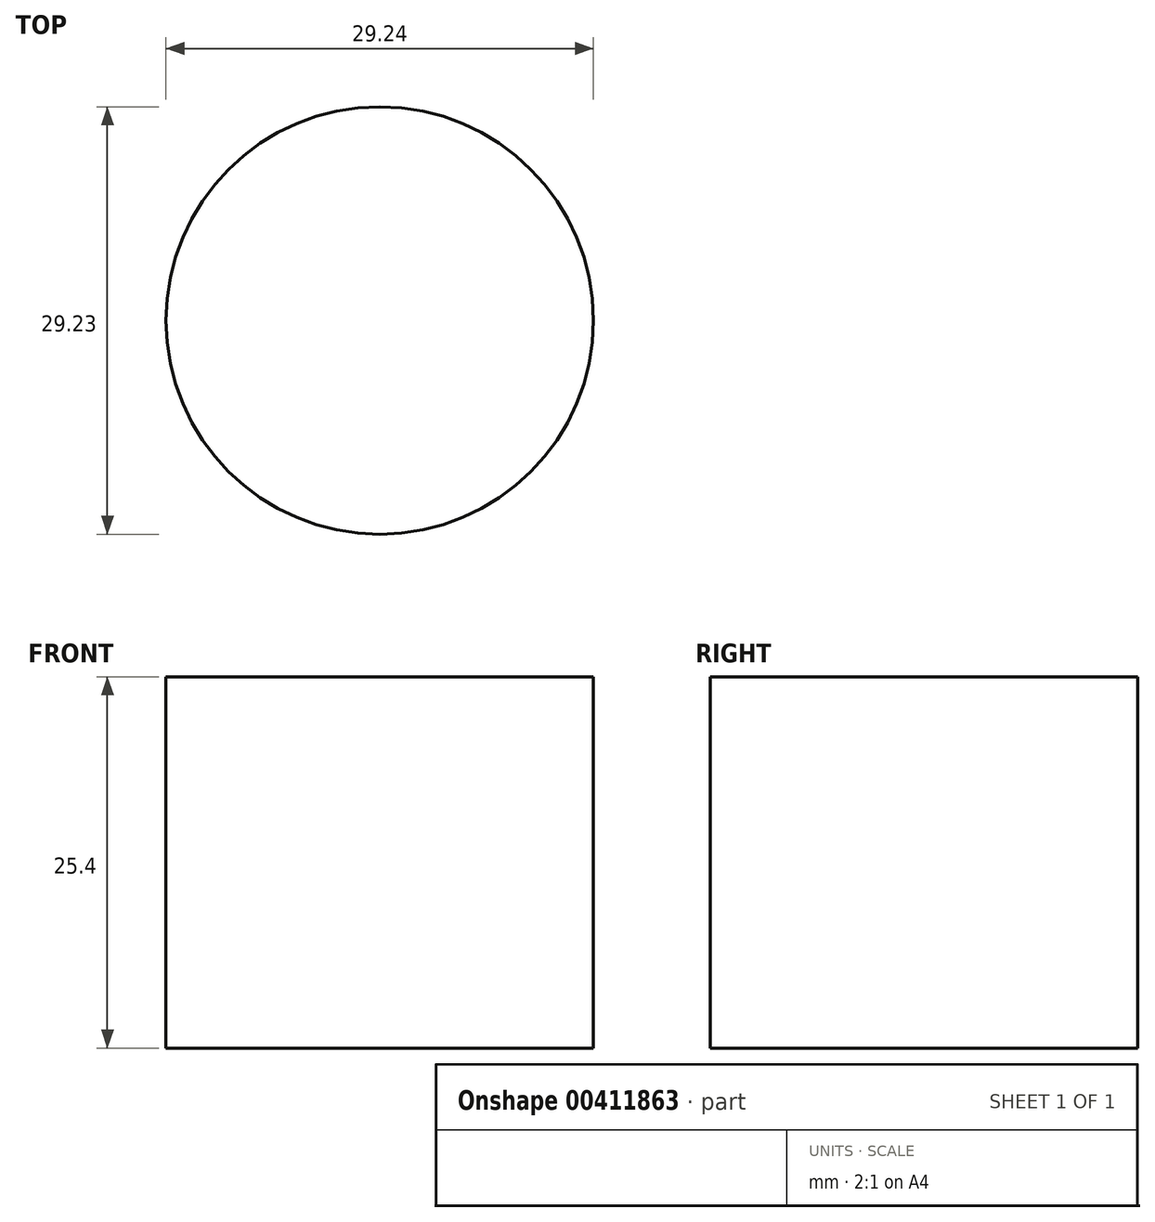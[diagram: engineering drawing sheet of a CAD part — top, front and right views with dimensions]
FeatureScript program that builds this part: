
annotation { "Feature Type Name" : "Feature", "Feature Type Description" : "" }
export const myFeature = defineFeature(function(context is Context, id is Id, definition is map)
    precondition{}
    {
        {
            var Q0;
            Q0=qCreatedBy(makeId("Top.planeOp"),FACE);
            var sketch = newSketch(context, id + "F0", { "sketchPlane" : qUnion([Q0])});
            skCircle(sketch, "E0", {"center": v(43.98, -20.7) * mm, "radius": 14.62 * mm});
            skCircle(sketch, "E1", {"center": v(0, 0) * mm, "radius": 6.66 * mm});
            skSolve(sketch);
        }
        {
            var Q0;
            Q0=makeQuery(id+"F0.imprint","IMPRINT",FACE,{"disambiguationData":[TD([[makeQuery(id+"F0.imprint","IMPRINT",EDGE,{"derivedFrom":sQuery(id+"F0.wireOp",EDGE,"E0")}),1.0]])]});
            extrude(context, id + "F1", {"entities" : qUnion([Q0]), "oppositeDirection" : true, "depth" : 25.4 * mm});
        }
    });
